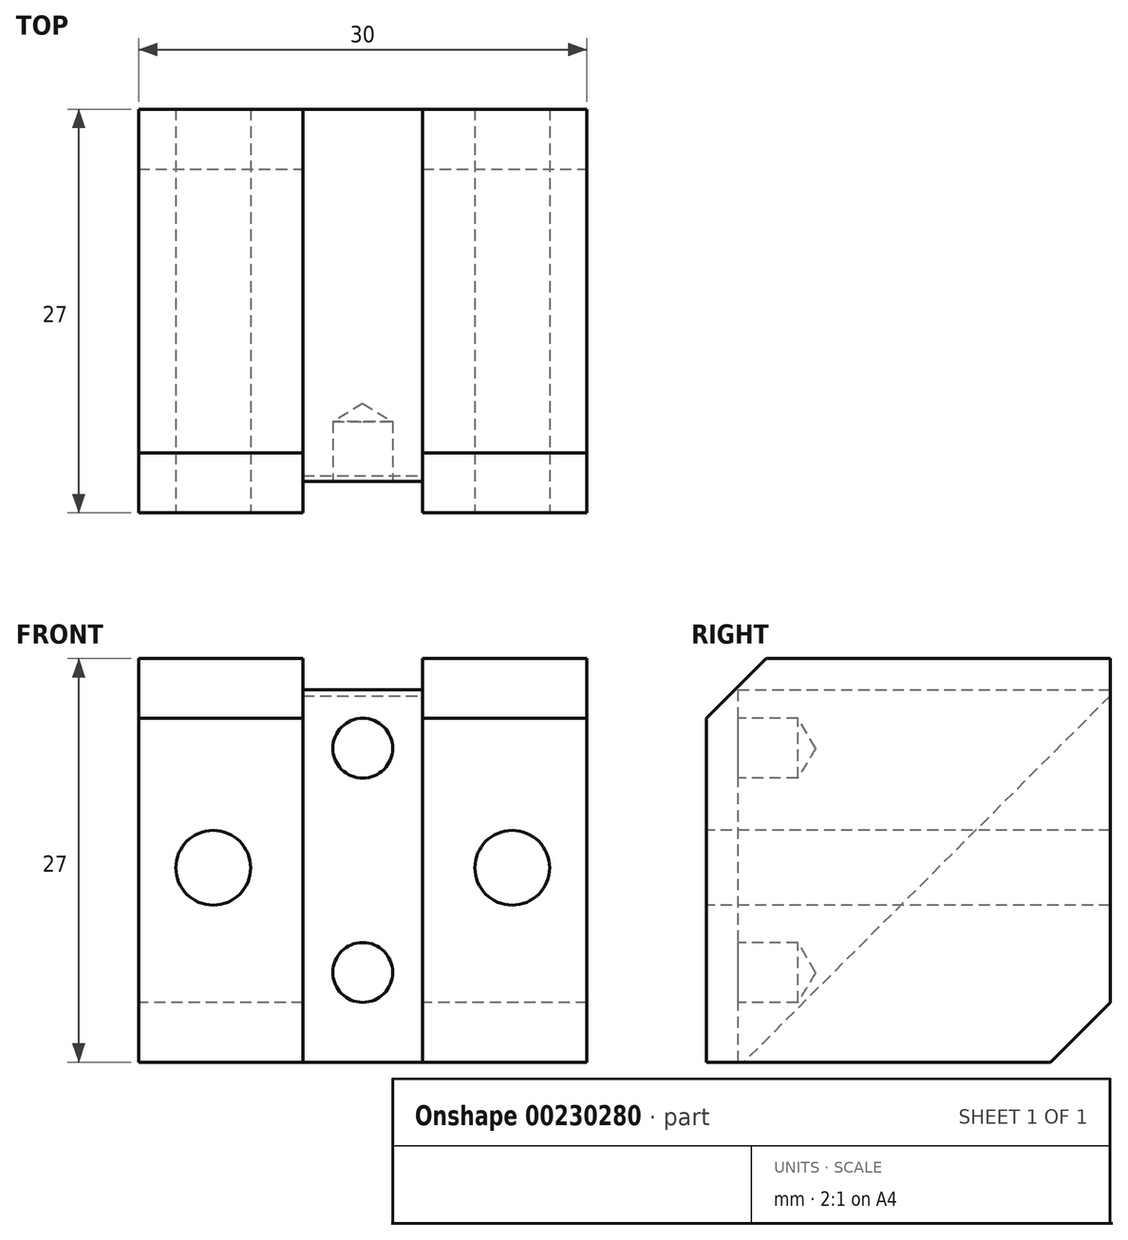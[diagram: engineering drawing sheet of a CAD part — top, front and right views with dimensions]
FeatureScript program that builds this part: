
annotation { "Feature Type Name" : "Feature", "Feature Type Description" : "" }
export const myFeature = defineFeature(function(context is Context, id is Id, definition is map)
    precondition{}
    {
        {
            var Q0;
            Q0=qCreatedBy(makeId("Front.planeOp"),FACE);
            var sketch = newSketch(context, id + "F0", { "sketchPlane" : qUnion([Q0])});
            skLineSegment(sketch, "E0.bottom", {"start": v(15, -13.5) * mm, "end": v(-15, -13.5) * mm});
            skLineSegment(sketch, "E0.top", {"start": v(15, 13.5) * mm, "end": v(-15, 13.5) * mm});
            skLineSegment(sketch, "E0.left", {"start": v(15, -13.5) * mm, "end": v(15, 13.5) * mm});
            skLineSegment(sketch, "E0.right", {"start": v(-15, -13.5) * mm, "end": v(-15, 13.5) * mm});
            skPoint(sketch, "E0.middle", {"position": v(0, 0) * mm});
            skSolve(sketch);
        }
        {
            var Q0;
            Q0=makeQuery(id+"F0.imprint","IMPRINT",FACE,{"disambiguationData":[TD([[makeQuery(id+"F0.imprint","IMPRINT",EDGE,{"derivedFrom":sQuery(id+"F0.wireOp",EDGE,"E0.bottom")}),-1.0]])]});
            extrude(context, id + "F1", {"entities" : qUnion([Q0]), "depth" : 27 * mm});
        }
        {
            var Q0;
            Q0=makeQuery(id+"F1.opExtrude","CAP_EDGE",EDGE,{"disambiguationData":[OSD([sQuery(id+"F0.wireOp",EDGE,"E0.bottom")])],"isStart":true});
            var Q1;
            Q1=makeQuery(id+"F1.opExtrude","CAP_EDGE",EDGE,{"disambiguationData":[OSD([sQuery(id+"F0.wireOp",EDGE,"E0.top")])],"isStart":false});
            chamfer(context, id + "F2", {"entities" : qUnion([Q0, Q1]), "width" : 4 * mm, "tangentPropagation" : true});
        }
        {
            var Q0;
            Q0=makeQuery(id+"F1.opExtrude","CAP_FACE",FACE,{"disambiguationData":[OSD([sQuery(id+"F0.wireOp",EDGE,"E0.bottom"),sQuery(id+"F0.wireOp",EDGE,"E0.top"),sQuery(id+"F0.wireOp",EDGE,"E0.left"),sQuery(id+"F0.wireOp",EDGE,"E0.right")])],"isStart":false});
            var sketch = newSketch(context, id + "F3", { "sketchPlane" : qUnion([Q0])});
            skPoint(sketch, "E1", {"position": v(-10, -0.5) * mm});
            skPoint(sketch, "E2", {"position": v(10, -0.5) * mm});
            skSolve(sketch);
        }
        {
            var Q0;
            Q0=sQuery(id+"F3.wireOp",VERTEX,"E1");
            var Q1;
            Q1=sQuery(id+"F3.wireOp",VERTEX,"E2");
            var Q2;
            Q2=makeQuery(id+"F1.opExtrude","SWEPT_BODY",BODY,{"disambiguationData":[OSD([sQuery(id+"F0.wireOp",EDGE,"E0.bottom"),sQuery(id+"F0.wireOp",EDGE,"E0.top"),sQuery(id+"F0.wireOp",EDGE,"E0.left"),sQuery(id+"F0.wireOp",EDGE,"E0.right")])]});
            hole(context, id + "F4", {"style" : HoleStyle.SIMPLE, "endStyle" : HoleEndStyle.THROUGH, "holeDiameter" : 5 * mm, "locations" : qUnion([Q0, Q1]), "scope" : qUnion([Q2]), "isTappedThrough" : true});
        }
        {
            var Q0;
            Q0=makeQuery(id+"F1.opExtrude","CAP_FACE",FACE,{"disambiguationData":[OSD([sQuery(id+"F0.wireOp",EDGE,"E0.bottom"),sQuery(id+"F0.wireOp",EDGE,"E0.top"),sQuery(id+"F0.wireOp",EDGE,"E0.left"),sQuery(id+"F0.wireOp",EDGE,"E0.right")])],"isStart":false});
            var sketch = newSketch(context, id + "F5", { "sketchPlane" : qUnion([Q0])});
            skLineSegment(sketch, "E3.bottom", {"start": v(4, -13.5) * mm, "end": v(-4, -13.5) * mm});
            skLineSegment(sketch, "E3.top", {"start": v(4, 13.5) * mm, "end": v(-4, 13.5) * mm});
            skLineSegment(sketch, "E3.left", {"start": v(4, -13.5) * mm, "end": v(4, 13.5) * mm});
            skLineSegment(sketch, "E3.right", {"start": v(-4, -13.5) * mm, "end": v(-4, 13.5) * mm});
            skPoint(sketch, "E3.middle", {"position": v(0, 0) * mm});
            skSolve(sketch);
        }
        {
            var Q0;
            {var subQ0=sQuery(id+"F5.wireOp",EDGE,"E3.bottom");Q0=makeQuery(id+"F5.imprint","IMPRINT",FACE,{"disambiguationData":[TD([[makeQuery(id+"F5.imprint","IMPRINT",EDGE,{"derivedFrom":subQ0}),-1.0]])]});}
            var Q1;
            {var subQ0=sQuery(id+"F5.wireOp",EDGE,"E3.top");Q1=makeQuery(id+"F5.imprint","IMPRINT",FACE,{"disambiguationData":[TD([[makeQuery(id+"F5.imprint","IMPRINT",EDGE,{"derivedFrom":subQ0}),1.0]])]});}
            extrude(context, id + "F6", {"entities" : qUnion([Q0, Q1]), "operationType" : NewBodyOperationType.REMOVE, "oppositeDirection" : true, "depth" : 2.1 * mm});
        }
        {
            var Q0;
            Q0=makeQuery(id+"F1.opExtrude","SWEPT_FACE",FACE,{"disambiguationData":[OSD([sQuery(id+"F0.wireOp",EDGE,"E0.top")])]});
            var sketch = newSketch(context, id + "F7", { "sketchPlane" : qUnion([Q0])});
            skLineSegment(sketch, "E4.bottom", {"start": v(4, -28.83) * mm, "end": v(-4, -28.83) * mm});
            skLineSegment(sketch, "E4.top", {"start": v(4, 28.83) * mm, "end": v(-4, 28.83) * mm});
            skLineSegment(sketch, "E4.left", {"start": v(4, -28.83) * mm, "end": v(4, 28.83) * mm});
            skLineSegment(sketch, "E4.right", {"start": v(-4, -28.83) * mm, "end": v(-4, 28.83) * mm});
            skPoint(sketch, "E4.middle", {"position": v(0, 0) * mm});
            skSolve(sketch);
        }
        {
            var Q0;
            {var subQ0=sQuery(id+"F7.wireOp",EDGE,"E4.top");Q0=makeQuery(id+"F7.imprint","IMPRINT",FACE,{"disambiguationData":[TD([[makeQuery(id+"F7.imprint","IMPRINT",EDGE,{"derivedFrom":subQ0}),1.0]])]});}
            var Q1;
            {var subQ0=sQuery(id+"F7.wireOp",EDGE,"E4.left");var subQ1=sQuery(id+"F0.wireOp",EDGE,"E0.top");var subQ4=makeQuery(id+"F1.opExtrude","CAP_EDGE",EDGE,{"disambiguationData":[OSD([subQ1])],"isStart":true});var subQ5=makeQuery(id+"F7.imprint","INTERSECT",VERTEX,{"derivedFrom":[subQ4,subQ0]});Q1=makeQuery(id+"F7.imprint","IMPRINT",FACE,{"disambiguationData":[TD([[makeQuery(id+"F7.imprint","IMPRINT",EDGE,{"disambiguationData":[TD([[subQ5,-1.0]])],"derivedFrom":subQ4}),1.0]])]});}
            var Q2;
            {var subQ0=sQuery(id+"F7.wireOp",EDGE,"E4.bottom");Q2=makeQuery(id+"F7.imprint","IMPRINT",FACE,{"disambiguationData":[TD([[makeQuery(id+"F7.imprint","IMPRINT",EDGE,{"derivedFrom":subQ0}),-1.0]])]});}
            extrude(context, id + "F8", {"entities" : qUnion([Q0, Q1, Q2]), "operationType" : NewBodyOperationType.REMOVE, "oppositeDirection" : true, "depth" : 2.1 * mm});
        }
        {
            var Q0;
            Q0=makeQuery(id+"F2.opChamfer","BLEND_FACE",FACE,{"disambiguationData":[OSD([sQuery(id+"F0.wireOp",EDGE,"E0.bottom")])]});
            var sketch = newSketch(context, id + "F9", { "sketchPlane" : qUnion([Q0])});
            skLineSegment(sketch, "E5.bottom", {"start": v(-4, 23.92) * mm, "end": v(4, 23.92) * mm});
            skLineSegment(sketch, "E5.top", {"start": v(-4, -46.08) * mm, "end": v(4, -46.08) * mm});
            skLineSegment(sketch, "E5.left", {"start": v(-4, 23.92) * mm, "end": v(-4, -46.08) * mm});
            skLineSegment(sketch, "E5.right", {"start": v(4, 23.92) * mm, "end": v(4, -46.08) * mm});
            skPoint(sketch, "E5.middle", {"position": v(0, -11.08) * mm});
            skPoint(sketch, "E5.middle.positionSnap0", {"position": v(0, -6.72) * mm});
            skPoint(sketch, "E5.centerSnap0", {"position": v(0, -6.72) * mm});
            skSolve(sketch);
        }
        {
            var Q0;
            {var subQ0=sQuery(id+"F9.wireOp",EDGE,"E5.top");Q0=makeQuery(id+"F9.imprint","IMPRINT",FACE,{"disambiguationData":[TD([[makeQuery(id+"F9.imprint","IMPRINT",EDGE,{"derivedFrom":subQ0}),1.0]])]});}
            var Q1;
            {var subQ0=sQuery(id+"F9.wireOp",EDGE,"E5.left");var subQ1=sQuery(id+"F0.wireOp",EDGE,"E0.bottom");var subQ2=makeQuery(id+"F1.opExtrude","CAP_EDGE",EDGE,{"disambiguationData":[OSD([subQ1])],"isStart":true});var subQ5=makeQuery(id+"F2.opChamfer","BLEND_EDGE",EDGE,{"blendedFrom":[subQ2,makeQuery(id+"F1.opExtrude","SWEPT_FACE",FACE,{"disambiguationData":[OSD([subQ1])]})],"blendedInto":[makeQuery(id+"F1.opExtrude","SWEPT_FACE",FACE,{"disambiguationData":[OSD([subQ1])]})]});var subQ6=makeQuery(id+"F9.imprint","INTERSECT",VERTEX,{"derivedFrom":[subQ5,subQ0]});Q1=makeQuery(id+"F9.imprint","IMPRINT",FACE,{"disambiguationData":[TD([[makeQuery(id+"F9.imprint","IMPRINT",EDGE,{"disambiguationData":[TD([[subQ6,1.0]])],"derivedFrom":subQ5}),-1.0]])]});}
            var Q2;
            {var subQ0=sQuery(id+"F9.wireOp",EDGE,"E5.bottom");Q2=makeQuery(id+"F9.imprint","IMPRINT",FACE,{"disambiguationData":[TD([[makeQuery(id+"F9.imprint","IMPRINT",EDGE,{"derivedFrom":subQ0}),-1.0]])]});}
            extrude(context, id + "F10", {"entities" : qUnion([Q0, Q1, Q2]), "operationType" : NewBodyOperationType.REMOVE, "oppositeDirection" : true, "depth" : 14.5 * mm});
        }
        {
            var Q0;
            Q0=makeQuery(id+"F6.boolean.opBoolean","COPY",FACE,{"derivedFrom":makeQuery(id+"F6.opExtrude","CAP_FACE",FACE,{"disambiguationData":[OSD([sQuery(id+"F5.wireOp",EDGE,"E3.bottom"),sQuery(id+"F5.wireOp",EDGE,"E3.top"),sQuery(id+"F5.wireOp",EDGE,"E3.left"),sQuery(id+"F5.wireOp",EDGE,"E3.right")])],"isStart":false})});
            var sketch = newSketch(context, id + "F11", { "sketchPlane" : qUnion([Q0])});
            skPoint(sketch, "E6", {"position": v(0, -7.5) * mm});
            skPoint(sketch, "E7", {"position": v(0, 7.5) * mm});
            skSolve(sketch);
        }
        {
            var Q0;
            Q0=sQuery(id+"F11.wireOp",VERTEX,"E6");
            var Q1;
            Q1=sQuery(id+"F11.wireOp",VERTEX,"E7");
            var Q2;
            Q2=makeQuery(id+"F1.opExtrude","SWEPT_BODY",BODY,{"disambiguationData":[OSD([sQuery(id+"F0.wireOp",EDGE,"E0.bottom"),sQuery(id+"F0.wireOp",EDGE,"E0.top"),sQuery(id+"F0.wireOp",EDGE,"E0.left"),sQuery(id+"F0.wireOp",EDGE,"E0.right")])]});
            hole(context, id + "F12", {"style" : HoleStyle.SIMPLE, "endStyle" : HoleEndStyle.BLIND, "holeDiameter" : 4 * mm, "holeDepth" : 4 * mm, "locations" : qUnion([Q0, Q1]), "scope" : qUnion([Q2])});
        }
    });
